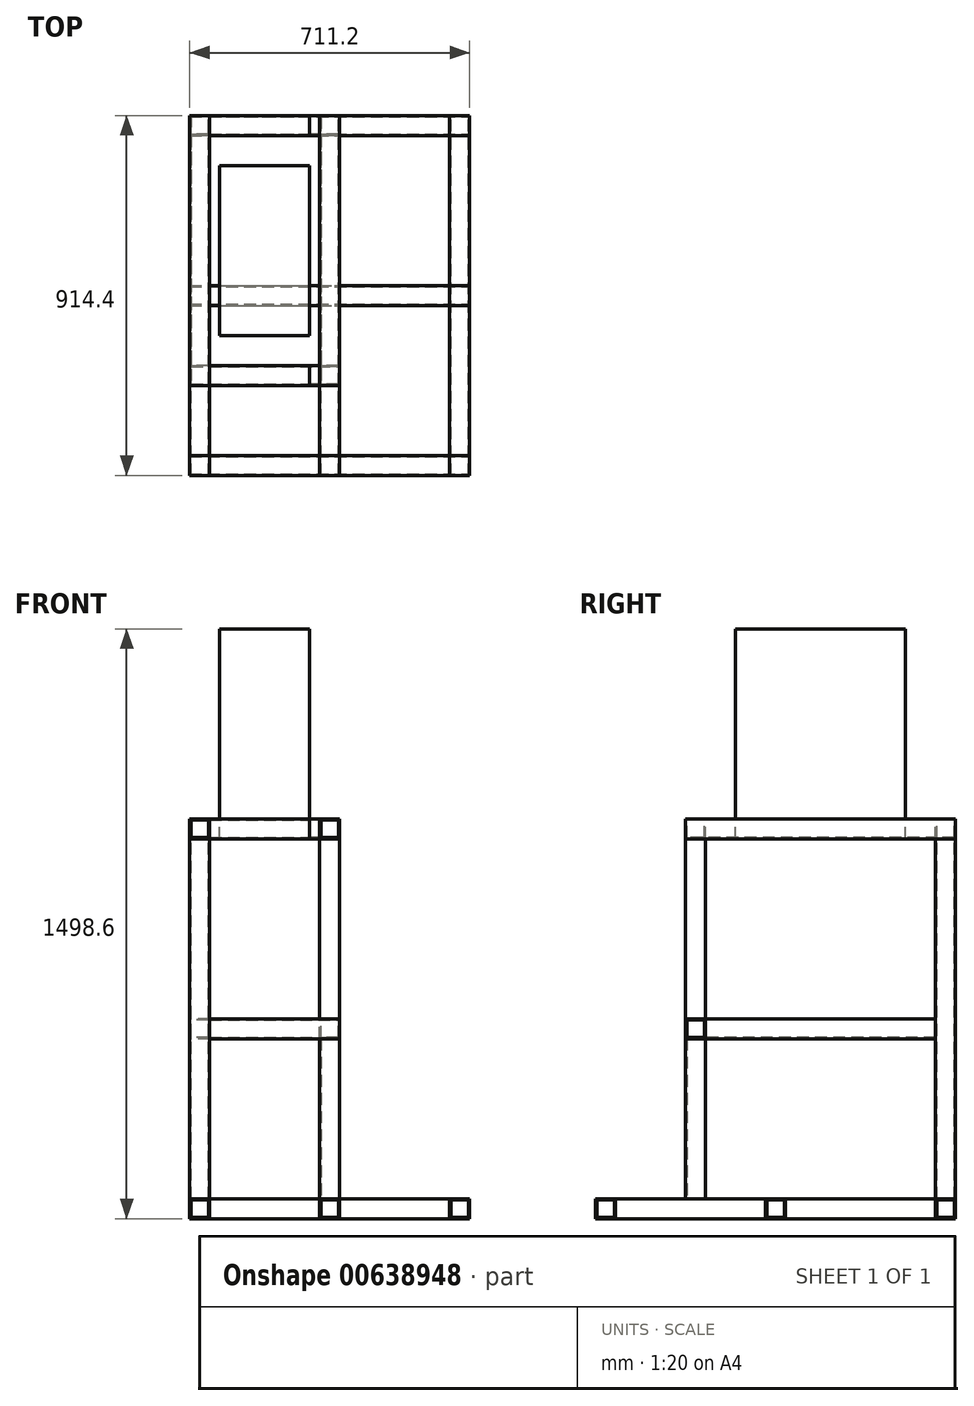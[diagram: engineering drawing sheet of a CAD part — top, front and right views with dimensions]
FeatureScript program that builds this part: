
annotation { "Feature Type Name" : "Feature", "Feature Type Description" : "" }
export const myFeature = defineFeature(function(context is Context, id is Id, definition is map)
    precondition{}
    {
        {
            var Q0;
            Q0=qCreatedBy(makeId("Front.planeOp"),FACE);
            var sketch = newSketch(context, id + "F0", { "sketchPlane" : qUnion([Q0])});
            skLineSegment(sketch, "E0.bottom", {"start": v(0, 0) * mm, "end": v(228.6, 0) * mm});
            skLineSegment(sketch, "E0.top", {"start": v(0, 533.4) * mm, "end": v(228.6, 533.4) * mm});
            skLineSegment(sketch, "E0.left", {"start": v(0, 0) * mm, "end": v(0, 533.4) * mm});
            skLineSegment(sketch, "E0.right", {"start": v(228.6, 0) * mm, "end": v(228.6, 533.4) * mm});
            skSolve(sketch);
        }
        {
            var Q0;
            Q0 = qSketchRegion(id + "F0", true);
            extrude(context, id + "F1", {"entities" : qUnion([Q0]), "depth" : 431.8 * mm, "offsetDistance" : 25.4 * mm});
        }
        {
            var Q0;
            Q0=makeQuery(id+"F1.opExtrude","SWEPT_FACE",FACE,{"disambiguationData":[OSD([sQuery(id+"F0.wireOp",EDGE,"E0.right")])]});
            var sketch = newSketch(context, id + "F2", { "sketchPlane" : qUnion([Q0])});
            skLineSegment(sketch, "E1.bottom", {"start": v(-508, 0) * mm, "end": v(-558.8, 0) * mm});
            skLineSegment(sketch, "E1.top", {"start": v(-508, 50.8) * mm, "end": v(-558.8, 50.8) * mm});
            skLineSegment(sketch, "E1.left", {"start": v(-508, 0) * mm, "end": v(-508, 50.8) * mm});
            skLineSegment(sketch, "E1.right", {"start": v(-558.8, 0) * mm, "end": v(-558.8, 50.8) * mm});
            skLineSegment(sketch, "E2.0", {"start": v(-555.62, 3.18) * mm, "end": v(-555.62, 47.62) * mm});
            skLineSegment(sketch, "E2.1", {"start": v(-511.18, 3.18) * mm, "end": v(-555.62, 3.18) * mm});
            skLineSegment(sketch, "E2.2", {"start": v(-511.18, 3.18) * mm, "end": v(-511.18, 47.62) * mm});
            skLineSegment(sketch, "E2.3", {"start": v(-511.18, 47.62) * mm, "end": v(-555.62, 47.62) * mm});
            skLineSegment(sketch, "E3.1.0.0", {"start": v(123.82, 3.18) * mm, "end": v(123.82, 47.63) * mm});
            skLineSegment(sketch, "E3.1.0.1", {"start": v(123.82, 3.18) * mm, "end": v(79.38, 3.18) * mm});
            skLineSegment(sketch, "E3.1.0.2", {"start": v(79.38, 3.18) * mm, "end": v(79.38, 47.62) * mm});
            skLineSegment(sketch, "E3.1.0.3", {"start": v(76.2, 0) * mm, "end": v(76.2, 50.8) * mm});
            skLineSegment(sketch, "E3.1.0.4", {"start": v(127, 0) * mm, "end": v(127, 50.8) * mm});
            skLineSegment(sketch, "E3.1.0.5", {"start": v(127, 50.8) * mm, "end": v(76.2, 50.8) * mm});
            skLineSegment(sketch, "E3.1.0.6", {"start": v(127, 0) * mm, "end": v(76.2, 0) * mm});
            skLineSegment(sketch, "E3.1.0.7", {"start": v(123.82, 47.62) * mm, "end": v(79.38, 47.62) * mm});
            skLineSegment(sketch, "E3.direction1", {"start": v(-558.8, 0) * mm, "end": v(76.2, 0) * mm, "construction": true});
            skSolve(sketch);
        }
        {
            var Q0;
            Q0 = qSketchRegion(id + "F2", true);
            extrude(context, id + "F3", {"entities" : qUnion([Q0]), "oppositeDirection" : true, "depth" : 254 * mm, "offsetDistance" : 25.4 * mm});
        }
        {
            var Q0;
            Q0 = qSketchRegion(id + "F2", true);
            extrude(context, id + "F4", {"entities" : qUnion([Q0]), "depth" : 25.4 * mm, "offsetDistance" : 25.4 * mm});
        }
        {
            var Q0;
            Q0=makeQuery(id+"F4.opExtrude","SWEPT_FACE",FACE,{"disambiguationData":[OSD([sQuery(id+"F2.wireOp",EDGE,"E1.right")])]});
            var sketch = newSketch(context, id + "F5", { "sketchPlane" : qUnion([Q0])});
            skLineSegment(sketch, "E4.bottom", {"start": v(254, 0) * mm, "end": v(304.8, 0) * mm});
            skLineSegment(sketch, "E4.top", {"start": v(254, 50.8) * mm, "end": v(304.8, 50.8) * mm});
            skLineSegment(sketch, "E4.left", {"start": v(254, 0) * mm, "end": v(254, 50.8) * mm});
            skLineSegment(sketch, "E4.right", {"start": v(304.8, 0) * mm, "end": v(304.8, 50.8) * mm});
            skLineSegment(sketch, "E5.bottom", {"start": v(-25.4, 0) * mm, "end": v(-76.2, 0) * mm});
            skLineSegment(sketch, "E5.top", {"start": v(-25.4, 50.8) * mm, "end": v(-76.2, 50.8) * mm});
            skLineSegment(sketch, "E5.left", {"start": v(-25.4, 0) * mm, "end": v(-25.4, 50.8) * mm});
            skLineSegment(sketch, "E5.right", {"start": v(-76.2, 0) * mm, "end": v(-76.2, 50.8) * mm});
            skLineSegment(sketch, "E6.0", {"start": v(257.18, 47.63) * mm, "end": v(301.63, 47.63) * mm});
            skLineSegment(sketch, "E6.1", {"start": v(257.18, 3.17) * mm, "end": v(257.18, 47.63) * mm});
            skLineSegment(sketch, "E6.2", {"start": v(257.18, 3.17) * mm, "end": v(301.63, 3.17) * mm});
            skLineSegment(sketch, "E6.3", {"start": v(301.63, 3.17) * mm, "end": v(301.63, 47.63) * mm});
            skLineSegment(sketch, "E7.0", {"start": v(-28.57, 3.18) * mm, "end": v(-73.02, 3.17) * mm});
            skLineSegment(sketch, "E7.1", {"start": v(-28.57, 3.18) * mm, "end": v(-28.57, 47.63) * mm});
            skLineSegment(sketch, "E7.2", {"start": v(-28.57, 47.63) * mm, "end": v(-73.02, 47.63) * mm});
            skLineSegment(sketch, "E7.3", {"start": v(-73.02, 3.17) * mm, "end": v(-73.02, 47.62) * mm});
            skSolve(sketch);
        }
        {
            var Q0;
            Q0 = qSketchRegion(id + "F5", true);
            extrude(context, id + "F6", {"entities" : qUnion([Q0]), "oppositeDirection" : true, "depth" : 685.8 * mm, "offsetDistance" : 25.4 * mm});
        }
        {
            var Q0;
            Q0=makeQuery(id+"F3.opExtrude","SWEPT_FACE",FACE,{"disambiguationData":[OSD([sQuery(id+"F2.wireOp",EDGE,"E3.1.0.6")])]});
            var sketch = newSketch(context, id + "F7", { "sketchPlane" : qUnion([Q0])});
            skLineSegment(sketch, "E8.bottom", {"start": v(-25.4, -76.2) * mm, "end": v(-76.2, -76.2) * mm});
            skLineSegment(sketch, "E8.top", {"start": v(-25.4, -127) * mm, "end": v(-76.2, -127) * mm});
            skLineSegment(sketch, "E8.left", {"start": v(-25.4, -76.2) * mm, "end": v(-25.4, -127) * mm});
            skLineSegment(sketch, "E8.right", {"start": v(-76.2, -76.2) * mm, "end": v(-76.2, -127) * mm});
            skLineSegment(sketch, "E9.bottom", {"start": v(304.8, -127) * mm, "end": v(254, -127) * mm});
            skLineSegment(sketch, "E9.top", {"start": v(304.8, -76.2) * mm, "end": v(254, -76.2) * mm});
            skLineSegment(sketch, "E9.left", {"start": v(304.8, -127) * mm, "end": v(304.8, -76.2) * mm});
            skLineSegment(sketch, "E9.right", {"start": v(254, -127) * mm, "end": v(254, -76.2) * mm});
            skLineSegment(sketch, "E10.bottom", {"start": v(-76.2, 558.8) * mm, "end": v(-25.4, 558.8) * mm});
            skLineSegment(sketch, "E10.top", {"start": v(-76.2, 508) * mm, "end": v(-25.4, 508) * mm});
            skLineSegment(sketch, "E10.left", {"start": v(-76.2, 558.8) * mm, "end": v(-76.2, 508) * mm});
            skLineSegment(sketch, "E10.right", {"start": v(-25.4, 558.8) * mm, "end": v(-25.4, 508) * mm});
            skLineSegment(sketch, "E11.0", {"start": v(301.63, -79.38) * mm, "end": v(257.18, -79.38) * mm});
            skLineSegment(sketch, "E11.1", {"start": v(301.63, -123.83) * mm, "end": v(301.63, -79.38) * mm});
            skLineSegment(sketch, "E11.2", {"start": v(301.63, -123.83) * mm, "end": v(257.18, -123.83) * mm});
            skLineSegment(sketch, "E11.3", {"start": v(257.18, -123.83) * mm, "end": v(257.18, -79.38) * mm});
            skLineSegment(sketch, "E12.0", {"start": v(-28.57, -79.38) * mm, "end": v(-28.57, -123.83) * mm});
            skLineSegment(sketch, "E12.1", {"start": v(-28.57, -79.38) * mm, "end": v(-73.02, -79.38) * mm});
            skLineSegment(sketch, "E12.2", {"start": v(-73.02, -79.38) * mm, "end": v(-73.02, -123.83) * mm});
            skLineSegment(sketch, "E12.3", {"start": v(-28.57, -123.83) * mm, "end": v(-73.02, -123.83) * mm});
            skLineSegment(sketch, "E13.0", {"start": v(-73.02, 555.62) * mm, "end": v(-28.58, 555.62) * mm});
            skLineSegment(sketch, "E13.1", {"start": v(-73.02, 555.62) * mm, "end": v(-73.02, 511.18) * mm});
            skLineSegment(sketch, "E13.2", {"start": v(-73.02, 511.18) * mm, "end": v(-28.58, 511.18) * mm});
            skLineSegment(sketch, "E13.3", {"start": v(-28.58, 555.62) * mm, "end": v(-28.58, 511.18) * mm});
            skSolve(sketch);
        }
        {
            var Q0;
            Q0 = qSketchRegion(id + "F7", true);
            extrude(context, id + "F8", {"entities" : qUnion([Q0]), "depth" : 914.4 * mm, "offsetDistance" : 25.4 * mm});
        }
        {
            var Q0;
            Q0=makeQuery(id+"F8.opExtrude","SWEPT_FACE",FACE,{"disambiguationData":[OSD([sQuery(id+"F7.wireOp",EDGE,"E8.top")])]});
            var sketch = newSketch(context, id + "F9", { "sketchPlane" : qUnion([Q0])});
            skLineSegment(sketch, "E14.bottom", {"start": v(76.2, -914.4) * mm, "end": v(25.4, -914.4) * mm});
            skLineSegment(sketch, "E14.top", {"start": v(76.2, -965.2) * mm, "end": v(25.4, -965.2) * mm});
            skLineSegment(sketch, "E14.left", {"start": v(76.2, -914.4) * mm, "end": v(76.2, -965.2) * mm});
            skLineSegment(sketch, "E14.right", {"start": v(25.4, -914.4) * mm, "end": v(25.4, -965.2) * mm});
            skLineSegment(sketch, "E15.0", {"start": v(73.02, -917.58) * mm, "end": v(73.02, -962.02) * mm});
            skLineSegment(sketch, "E15.1", {"start": v(73.02, -917.58) * mm, "end": v(28.57, -917.58) * mm});
            skLineSegment(sketch, "E15.2", {"start": v(28.57, -917.58) * mm, "end": v(28.57, -962.02) * mm});
            skLineSegment(sketch, "E15.3", {"start": v(73.02, -962.02) * mm, "end": v(28.57, -962.02) * mm});
            skLineSegment(sketch, "E16.1.0.0", {"start": v(-304.8, -914.4) * mm, "end": v(-304.8, -965.2) * mm});
            skLineSegment(sketch, "E16.1.0.1", {"start": v(-257.18, -917.58) * mm, "end": v(-301.63, -917.58) * mm});
            skLineSegment(sketch, "E16.1.0.2", {"start": v(-257.18, -962.02) * mm, "end": v(-301.63, -962.02) * mm});
            skLineSegment(sketch, "E16.1.0.3", {"start": v(-301.63, -917.58) * mm, "end": v(-301.63, -962.02) * mm});
            skLineSegment(sketch, "E16.1.0.4", {"start": v(-254, -965.2) * mm, "end": v(-304.8, -965.2) * mm});
            skLineSegment(sketch, "E16.1.0.5", {"start": v(-257.18, -917.58) * mm, "end": v(-257.18, -962.02) * mm});
            skLineSegment(sketch, "E16.1.0.6", {"start": v(-254, -914.4) * mm, "end": v(-304.8, -914.4) * mm});
            skLineSegment(sketch, "E16.1.0.7", {"start": v(-254, -914.4) * mm, "end": v(-254, -965.2) * mm});
            skLineSegment(sketch, "E16.2.0.0", {"start": v(-635, -914.4) * mm, "end": v(-635, -965.2) * mm});
            skLineSegment(sketch, "E16.2.0.1", {"start": v(-587.38, -917.58) * mm, "end": v(-631.83, -917.58) * mm});
            skLineSegment(sketch, "E16.2.0.2", {"start": v(-587.38, -962.02) * mm, "end": v(-631.83, -962.02) * mm});
            skLineSegment(sketch, "E16.2.0.3", {"start": v(-631.83, -917.58) * mm, "end": v(-631.83, -962.02) * mm});
            skLineSegment(sketch, "E16.2.0.4", {"start": v(-584.2, -965.2) * mm, "end": v(-635, -965.2) * mm});
            skLineSegment(sketch, "E16.2.0.5", {"start": v(-587.38, -917.58) * mm, "end": v(-587.38, -962.02) * mm});
            skLineSegment(sketch, "E16.2.0.6", {"start": v(-584.2, -914.4) * mm, "end": v(-635, -914.4) * mm});
            skLineSegment(sketch, "E16.2.0.7", {"start": v(-584.2, -914.4) * mm, "end": v(-584.2, -965.2) * mm});
            skLineSegment(sketch, "E16.direction1", {"start": v(25.4, -965.2) * mm, "end": v(-304.8, -965.2) * mm, "construction": true});
            skSolve(sketch);
        }
        {
            var Q0;
            Q0 = qSketchRegion(id + "F9", true);
            extrude(context, id + "F10", {"entities" : qUnion([Q0]), "oppositeDirection" : true, "depth" : 914.4 * mm, "offsetDistance" : 25.4 * mm});
        }
        {
            var Q0;
            Q0=makeQuery(id+"F10.opExtrude","SWEPT_FACE",FACE,{"disambiguationData":[OSD([sQuery(id+"F9.wireOp",EDGE,"E16.2.0.0")])]});
            var sketch = newSketch(context, id + "F11", { "sketchPlane" : qUnion([Q0])});
            skLineSegment(sketch, "E17.bottom", {"start": v(127, -914.4) * mm, "end": v(76.2, -914.4) * mm});
            skLineSegment(sketch, "E17.top", {"start": v(127, -965.2) * mm, "end": v(76.2, -965.2) * mm});
            skLineSegment(sketch, "E17.left", {"start": v(127, -914.4) * mm, "end": v(127, -965.2) * mm});
            skLineSegment(sketch, "E17.right", {"start": v(76.2, -914.4) * mm, "end": v(76.2, -965.2) * mm});
            skLineSegment(sketch, "E18.0", {"start": v(79.38, -917.57) * mm, "end": v(79.38, -962.02) * mm});
            skLineSegment(sketch, "E18.1", {"start": v(123.83, -917.57) * mm, "end": v(79.38, -917.57) * mm});
            skLineSegment(sketch, "E18.2", {"start": v(123.83, -917.57) * mm, "end": v(123.83, -962.02) * mm});
            skLineSegment(sketch, "E18.3", {"start": v(123.83, -962.02) * mm, "end": v(79.38, -962.02) * mm});
            skLineSegment(sketch, "E19.1.0.0", {"start": v(-304.8, -914.4) * mm, "end": v(-355.6, -914.4) * mm});
            skLineSegment(sketch, "E19.1.0.1", {"start": v(-304.8, -965.2) * mm, "end": v(-355.6, -965.2) * mm});
            skLineSegment(sketch, "E19.1.0.2", {"start": v(-304.8, -914.4) * mm, "end": v(-304.8, -965.2) * mm});
            skLineSegment(sketch, "E19.1.0.3", {"start": v(-307.97, -962.02) * mm, "end": v(-352.42, -962.02) * mm});
            skLineSegment(sketch, "E19.1.0.4", {"start": v(-307.97, -917.57) * mm, "end": v(-307.97, -962.02) * mm});
            skLineSegment(sketch, "E19.1.0.5", {"start": v(-307.97, -917.57) * mm, "end": v(-352.42, -917.57) * mm});
            skLineSegment(sketch, "E19.1.0.6", {"start": v(-352.42, -917.57) * mm, "end": v(-352.42, -962.02) * mm});
            skLineSegment(sketch, "E19.1.0.7", {"start": v(-355.6, -914.4) * mm, "end": v(-355.6, -965.2) * mm});
            skLineSegment(sketch, "E19.2.0.0", {"start": v(-736.6, -914.4) * mm, "end": v(-787.4, -914.4) * mm});
            skLineSegment(sketch, "E19.2.0.1", {"start": v(-736.6, -965.2) * mm, "end": v(-787.4, -965.2) * mm});
            skLineSegment(sketch, "E19.2.0.2", {"start": v(-736.6, -914.4) * mm, "end": v(-736.6, -965.2) * mm});
            skLineSegment(sketch, "E19.2.0.3", {"start": v(-739.77, -962.02) * mm, "end": v(-784.22, -962.02) * mm});
            skLineSegment(sketch, "E19.2.0.4", {"start": v(-739.77, -917.58) * mm, "end": v(-739.77, -962.02) * mm});
            skLineSegment(sketch, "E19.2.0.5", {"start": v(-739.77, -917.57) * mm, "end": v(-784.22, -917.57) * mm});
            skLineSegment(sketch, "E19.2.0.6", {"start": v(-784.22, -917.58) * mm, "end": v(-784.22, -962.02) * mm});
            skLineSegment(sketch, "E19.2.0.7", {"start": v(-787.4, -914.4) * mm, "end": v(-787.4, -965.2) * mm});
            skLineSegment(sketch, "E19.direction1", {"start": v(76.2, -965.2) * mm, "end": v(-355.6, -965.2) * mm, "construction": true});
            skSolve(sketch);
        }
        {
            var Q0;
            Q0 = qSketchRegion(id + "F11", true);
            extrude(context, id + "F12", {"entities" : qUnion([Q0]), "oppositeDirection" : true, "depth" : 711.2 * mm, "offsetDistance" : 25.4 * mm});
        }
        {
            var Q0;
            Q0=makeQuery(id+"F10.opExtrude","SWEPT_FACE",FACE,{"disambiguationData":[OSD([sQuery(id+"F9.wireOp",EDGE,"E16.1.0.6")])]});
            var sketch = newSketch(context, id + "F13", { "sketchPlane" : qUnion([Q0])});
            skLineSegment(sketch, "E20.bottom", {"start": v(304.8, -508) * mm, "end": v(254, -508) * mm});
            skLineSegment(sketch, "E20.top", {"start": v(304.8, -558.8) * mm, "end": v(254, -558.8) * mm});
            skLineSegment(sketch, "E20.left", {"start": v(304.8, -508) * mm, "end": v(304.8, -558.8) * mm});
            skLineSegment(sketch, "E20.right", {"start": v(254, -508) * mm, "end": v(254, -558.8) * mm});
            skLineSegment(sketch, "E21.0", {"start": v(301.63, -511.18) * mm, "end": v(257.18, -511.18) * mm});
            skLineSegment(sketch, "E21.1", {"start": v(301.63, -511.18) * mm, "end": v(301.63, -555.62) * mm});
            skLineSegment(sketch, "E21.2", {"start": v(301.63, -555.62) * mm, "end": v(257.18, -555.62) * mm});
            skLineSegment(sketch, "E21.3", {"start": v(257.18, -511.18) * mm, "end": v(257.18, -555.62) * mm});
            skSolve(sketch);
        }
        {
            var Q0;
            Q0 = qSketchRegion(id + "F13", true);
            extrude(context, id + "F14", {"entities" : qUnion([Q0]), "operationType" : NewBodyOperationType.ADD, "depth" : 406.4 * mm, "offsetDistance" : 25.4 * mm});
        }
        {
            var Q0;
            Q0=makeQuery(id+"F14.boolean.opBoolean","MERGE",FACE,{"derivedFrom":[makeQuery(id+"F10.opExtrude","SWEPT_FACE",FACE,{"disambiguationData":[OSD([sQuery(id+"F9.wireOp",EDGE,"E16.1.0.0")])]}),makeQuery(id+"F14.opExtrude","SWEPT_FACE",FACE,{"disambiguationData":[OSD([sQuery(id+"F13.wireOp",EDGE,"E20.left")])]})]});
            var sketch = newSketch(context, id + "F15", { "sketchPlane" : qUnion([Q0])});
            skLineSegment(sketch, "E22.bottom", {"start": v(-558.8, -508) * mm, "end": v(-508, -508) * mm});
            skLineSegment(sketch, "E22.top", {"start": v(-558.8, -457.2) * mm, "end": v(-508, -457.2) * mm});
            skLineSegment(sketch, "E22.left", {"start": v(-558.8, -508) * mm, "end": v(-558.8, -457.2) * mm});
            skLineSegment(sketch, "E22.right", {"start": v(-508, -508) * mm, "end": v(-508, -457.2) * mm});
            skLineSegment(sketch, "E23.0", {"start": v(-555.62, -504.82) * mm, "end": v(-511.18, -504.82) * mm});
            skLineSegment(sketch, "E23.1", {"start": v(-555.62, -504.82) * mm, "end": v(-555.62, -460.37) * mm});
            skLineSegment(sketch, "E23.2", {"start": v(-555.62, -460.37) * mm, "end": v(-511.18, -460.37) * mm});
            skLineSegment(sketch, "E23.3", {"start": v(-511.18, -504.82) * mm, "end": v(-511.18, -460.37) * mm});
            skSolve(sketch);
        }
        {
            var Q0;
            Q0 = qSketchRegion(id + "F15", true);
            extrude(context, id + "F16", {"entities" : qUnion([Q0]), "oppositeDirection" : true, "depth" : 330.2 * mm, "offsetDistance" : 25.4 * mm});
        }
        {
            var Q0;
            Q0=makeQuery(id+"F16.opExtrude","SWEPT_FACE",FACE,{"disambiguationData":[OSD([sQuery(id+"F15.wireOp",EDGE,"E22.right")])]});
            var sketch = newSketch(context, id + "F17", { "sketchPlane" : qUnion([Q0])});
            skLineSegment(sketch, "E24.bottom", {"start": v(-304.8, -508) * mm, "end": v(-254, -508) * mm});
            skLineSegment(sketch, "E24.top", {"start": v(-304.8, -457.2) * mm, "end": v(-254, -457.2) * mm});
            skLineSegment(sketch, "E24.left", {"start": v(-304.8, -508) * mm, "end": v(-304.8, -457.2) * mm});
            skLineSegment(sketch, "E24.right", {"start": v(-254, -508) * mm, "end": v(-254, -457.2) * mm});
            skLineSegment(sketch, "E25.0", {"start": v(-301.63, -504.82) * mm, "end": v(-257.18, -504.82) * mm});
            skLineSegment(sketch, "E25.1", {"start": v(-301.63, -504.82) * mm, "end": v(-301.63, -460.38) * mm});
            skLineSegment(sketch, "E25.2", {"start": v(-301.63, -460.38) * mm, "end": v(-257.18, -460.38) * mm});
            skLineSegment(sketch, "E25.3", {"start": v(-257.18, -504.82) * mm, "end": v(-257.18, -460.38) * mm});
            skLineSegment(sketch, "E26.1.0.0", {"start": v(28.57, -504.82) * mm, "end": v(73.02, -504.82) * mm});
            skLineSegment(sketch, "E26.1.0.1", {"start": v(28.57, -504.82) * mm, "end": v(28.57, -460.38) * mm});
            skLineSegment(sketch, "E26.1.0.2", {"start": v(76.2, -508) * mm, "end": v(76.2, -457.2) * mm});
            skLineSegment(sketch, "E26.1.0.3", {"start": v(73.02, -504.82) * mm, "end": v(73.02, -460.38) * mm});
            skLineSegment(sketch, "E26.1.0.4", {"start": v(25.4, -508) * mm, "end": v(76.2, -508) * mm});
            skLineSegment(sketch, "E26.1.0.5", {"start": v(25.4, -457.2) * mm, "end": v(76.2, -457.2) * mm});
            skLineSegment(sketch, "E26.1.0.6", {"start": v(25.4, -508) * mm, "end": v(25.4, -457.2) * mm});
            skLineSegment(sketch, "E26.1.0.7", {"start": v(28.57, -460.38) * mm, "end": v(73.02, -460.38) * mm});
            skLineSegment(sketch, "E26.direction1", {"start": v(-304.8, -508) * mm, "end": v(25.4, -508) * mm, "construction": true});
            skSolve(sketch);
        }
        {
            var Q0;
            Q0 = qSketchRegion(id + "F17", true);
            extrude(context, id + "F18", {"entities" : qUnion([Q0]), "depth" : 584.2 * mm, "offsetDistance" : 25.4 * mm});
        }
    });
